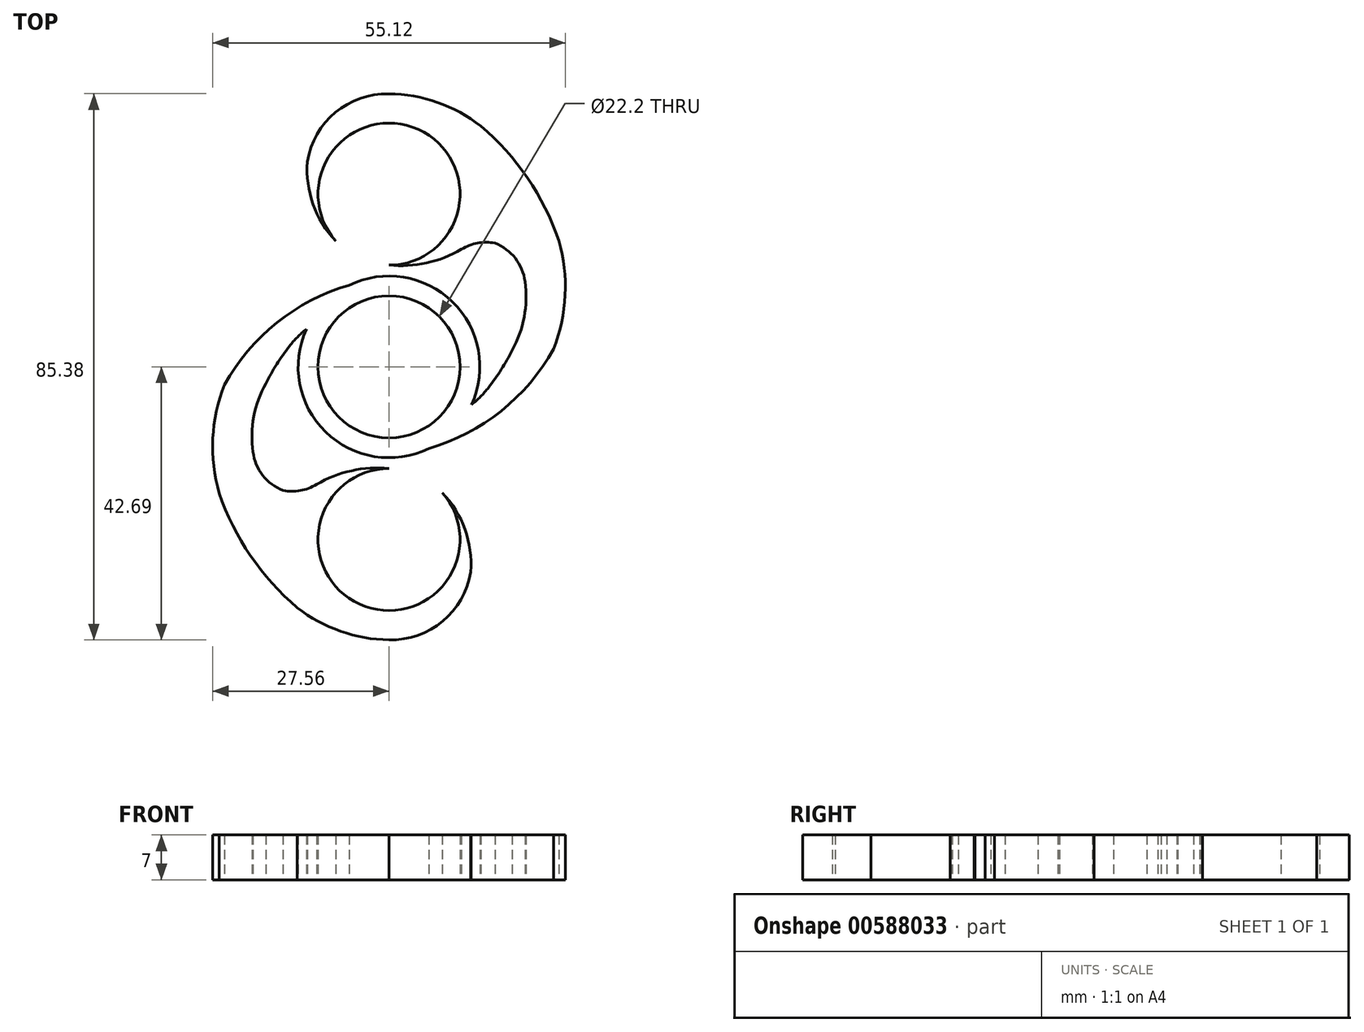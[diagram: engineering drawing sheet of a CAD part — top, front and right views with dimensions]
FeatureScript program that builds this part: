
annotation { "Feature Type Name" : "Feature", "Feature Type Description" : "" }
export const myFeature = defineFeature(function(context is Context, id is Id, definition is map)
    precondition{}
    {
        {
            var Q0;
            Q0=qCreatedBy(makeId("Top.planeOp"),FACE);
            var sketch = newSketch(context, id + "F0", { "sketchPlane" : qUnion([Q0])});
            skCircle(sketch, "E0", {"center": v(0, 0) * mm, "radius": 11.1 * mm});
            skArc(sketch, "E1", {"start": v(0, 15.9) * mm, "mid": v(4.58, 37.11) * mm, "end": v(-8.34, 19.68) * mm});
            skArc(sketch, "E2.1.0", {"start": v(0, -15.9) * mm, "mid": v(-4.58, -37.11) * mm, "end": v(8.34, -19.68) * mm});
            skArc(sketch, "E3", {"start": v(-12.77, 32.05) * mm, "mid": v(-11.86, 25.4) * mm, "end": v(-8.34, 19.68) * mm});
            skArc(sketch, "E4", {"start": v(0, 42.68) * mm, "mid": v(-8.38, 39.77) * mm, "end": v(-12.77, 32.05) * mm});
            skArc(sketch, "E5", {"start": v(14.32, 37.65) * mm, "mid": v(7.57, 41.34) * mm, "end": v(0, 42.68) * mm});
            skArc(sketch, "E6", {"start": v(26.54, 19.75) * mm, "mid": v(21.64, 29.53) * mm, "end": v(14.32, 37.65) * mm});
            skArc(sketch, "E7", {"start": v(6.22, -12.76) * mm, "mid": v(17.51, -6.9) * mm, "end": v(25.73, 2.8) * mm});
            skArc(sketch, "E8.0", {"start": v(-12.91, 5.9) * mm, "mid": v(-9.92, -10.16) * mm, "end": v(6.22, -12.76) * mm});
            skArc(sketch, "E9", {"start": v(25.73, 2.8) * mm, "mid": v(27.53, 11.2) * mm, "end": v(26.54, 19.75) * mm});
            skArc(sketch, "E10.1.0", {"start": v(12.77, -32.05) * mm, "mid": v(11.86, -25.4) * mm, "end": v(8.34, -19.68) * mm});
            skArc(sketch, "E10.1.1", {"start": v(0, -42.68) * mm, "mid": v(8.38, -39.77) * mm, "end": v(12.77, -32.05) * mm});
            skArc(sketch, "E10.1.2", {"start": v(-14.32, -37.65) * mm, "mid": v(-7.57, -41.34) * mm, "end": v(0, -42.68) * mm});
            skArc(sketch, "E10.1.3", {"start": v(-26.54, -19.75) * mm, "mid": v(-21.64, -29.53) * mm, "end": v(-14.32, -37.65) * mm});
            skArc(sketch, "E10.1.4", {"start": v(-25.73, -2.8) * mm, "mid": v(-27.53, -11.2) * mm, "end": v(-26.54, -19.75) * mm});
            skArc(sketch, "E10.1.5", {"start": v(-6.22, 12.76) * mm, "mid": v(-17.51, 6.9) * mm, "end": v(-25.73, -2.8) * mm});
            skArc(sketch, "E11", {"start": v(0, 15.9) * mm, "mid": v(5.94, 16.26) * mm, "end": v(11.46, 18.47) * mm});
            skArc(sketch, "E12", {"start": v(21.25, 13.32) * mm, "mid": v(19.73, 16.97) * mm, "end": v(16.55, 19.34) * mm});
            skArc(sketch, "E13", {"start": v(12.91, -5.9) * mm, "mid": v(14.32, -4.65) * mm, "end": v(15.55, -3.23) * mm});
            skArc(sketch, "E14", {"start": v(16.55, 19.34) * mm, "mid": v(13.85, 19.35) * mm, "end": v(11.32, 18.38) * mm});
            skArc(sketch, "E15", {"start": v(19.25, 2.6) * mm, "mid": v(21.13, 7.8) * mm, "end": v(21.25, 13.32) * mm});
            skArc(sketch, "E16", {"start": v(15.22, -3.65) * mm, "mid": v(17.4, -0.64) * mm, "end": v(19.25, 2.6) * mm});
            skPoint(sketch, "E17.orphan", {"position": v(17.47, 0) * mm});
            skArc(sketch, "E18.1.0", {"start": v(0, -15.9) * mm, "mid": v(-5.94, -16.26) * mm, "end": v(-11.46, -18.47) * mm});
            skArc(sketch, "E18.1.1", {"start": v(-16.55, -19.34) * mm, "mid": v(-13.85, -19.35) * mm, "end": v(-11.32, -18.38) * mm});
            skArc(sketch, "E18.1.2", {"start": v(-21.25, -13.32) * mm, "mid": v(-19.73, -16.97) * mm, "end": v(-16.55, -19.34) * mm});
            skArc(sketch, "E18.1.3", {"start": v(-19.25, -2.6) * mm, "mid": v(-21.13, -7.8) * mm, "end": v(-21.25, -13.32) * mm});
            skArc(sketch, "E18.1.4", {"start": v(-15.22, 3.65) * mm, "mid": v(-17.4, 0.64) * mm, "end": v(-19.25, -2.6) * mm});
            skArc(sketch, "E18.1.5", {"start": v(-12.91, 5.9) * mm, "mid": v(-14.32, 4.65) * mm, "end": v(-15.55, 3.23) * mm});
            skArc(sketch, "E19.trimOffspring", {"start": v(12.91, -5.9) * mm, "mid": v(9.92, 10.16) * mm, "end": v(-6.22, 12.76) * mm});
            skSolve(sketch);
        }
        {
            var Q0;
            Q0=makeQuery(id+"F0.imprint","IMPRINT",FACE,{"disambiguationData":[TD([[makeQuery(id+"F0.imprint","IMPRINT",EDGE,{"derivedFrom":sQuery(id+"F0.wireOp",EDGE,"E0")}),-1.0]])]});
            extrude(context, id + "F1", {"entities" : qUnion([Q0]), "depth" : 7 * mm, "offsetDistance" : 25 * mm});
        }
    });
